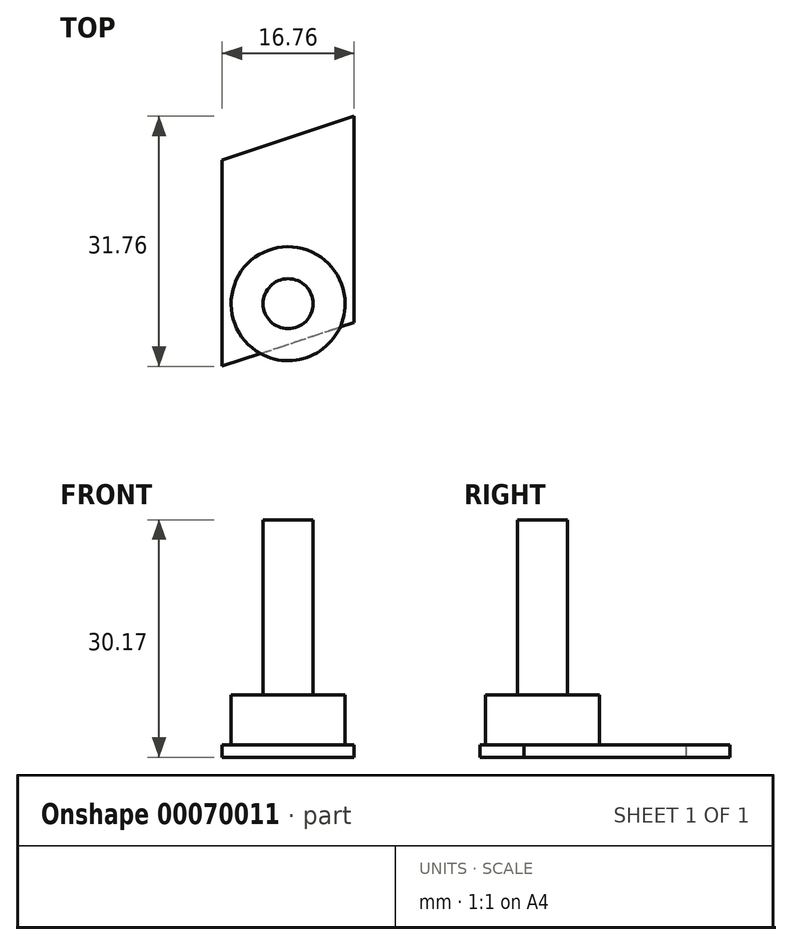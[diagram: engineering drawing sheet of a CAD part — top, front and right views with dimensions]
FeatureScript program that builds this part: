
annotation { "Feature Type Name" : "Feature", "Feature Type Description" : "" }
export const myFeature = defineFeature(function(context is Context, id is Id, definition is map)
    precondition{}
    {
        {
            var Q0;
            Q0=qCreatedBy(makeId("Top.planeOp"),FACE);
            var sketch = newSketch(context, id + "F0", { "sketchPlane" : qUnion([Q0])});
            skLineSegment(sketch, "E0.bottom", {"start": v(-8.38, 15.88) * mm, "end": v(8.38, 15.88) * mm, "construction": true});
            skLineSegment(sketch, "E0.top", {"start": v(-8.38, -15.88) * mm, "end": v(8.38, -15.88) * mm, "construction": true});
            skLineSegment(sketch, "E0.left", {"start": v(-8.38, 15.88) * mm, "end": v(-8.38, -15.88) * mm, "construction": true});
            skLineSegment(sketch, "E0.right", {"start": v(8.38, 15.88) * mm, "end": v(8.38, -15.88) * mm, "construction": true});
            skPoint(sketch, "E0.middle", {"position": v(0, 0) * mm});
            skLineSegment(sketch, "E1", {"start": v(8.38, 15.88) * mm, "end": v(-8.38, 10.32) * mm});
            skLineSegment(sketch, "E2", {"start": v(-8.38, -15.88) * mm, "end": v(8.38, -10.32) * mm});
            skLineSegment(sketch, "E3", {"start": v(-8.38, 10.32) * mm, "end": v(-8.38, -15.88) * mm});
            skLineSegment(sketch, "E4", {"start": v(8.38, -10.32) * mm, "end": v(8.38, 15.88) * mm});
            skCircle(sketch, "E5", {"center": v(0, -7.94) * mm, "radius": 7.24 * mm, "construction": true});
            skCircle(sketch, "E6", {"center": v(0, -7.94) * mm, "radius": 3.18 * mm, "construction": true});
            skLineSegment(sketch, "E7", {"start": v(-8.38, 0) * mm, "end": v(8.38, 0) * mm, "construction": true});
            skLineSegment(sketch, "E8", {"start": v(0, 0) * mm, "end": v(0, -15.88) * mm, "construction": true});
            skSolve(sketch);
        }
        {
            var Q0;
            Q0 = qSketchRegion(id + "F0", true);
            extrude(context, id + "F1", {"entities" : qUnion([Q0]), "oppositeDirection" : true, "depth" : 1.59 * mm});
        }
        {
            var Q0;
            Q0=makeQuery(id+"F0.imprint","IMPRINT",FACE,{"disambiguationData":[TD([[makeQuery(id+"F0.imprint","IMPRINT",EDGE,{"derivedFrom":sQuery(id+"F0.wireOp",EDGE,"E1")}),1.0]])]});
            var sketch = newSketch(context, id + "F2", { "sketchPlane" : qUnion([Q0])});
            skCircle(sketch, "E9.0", {"center": v(0, -7.94) * mm, "radius": 7.24 * mm});
            skSolve(sketch);
        }
        {
            var Q0;
            {var subQ0=sQuery(id+"F2.wireOp",EDGE,"E9.0");var subQ1=makeQuery(id+"F0.imprint","IMPRINT",EDGE,{"derivedFrom":sQuery(id+"F0.wireOp",EDGE,"E2")});var subQ2=makeQuery(id+"F2.imprint","INTERSECT",VERTEX,{"disambiguationData":[OD(0.0)],"derivedFrom":[subQ1,subQ0]});Q0=makeQuery(id+"F2.imprint","IMPRINT",FACE,{"disambiguationData":[TD([[makeQuery(id+"F2.imprint","IMPRINT",EDGE,{"disambiguationData":[TD([[subQ2,1.0]])],"derivedFrom":subQ0}),1.0]])]});}
            var Q1;
            {var subQ0=sQuery(id+"F2.wireOp",EDGE,"E9.0");var subQ1=makeQuery(id+"F0.imprint","IMPRINT",EDGE,{"derivedFrom":sQuery(id+"F0.wireOp",EDGE,"E2")});var subQ2=makeQuery(id+"F2.imprint","INTERSECT",VERTEX,{"disambiguationData":[OD(0.0)],"derivedFrom":[subQ1,subQ0]});Q1=makeQuery(id+"F2.imprint","IMPRINT",FACE,{"disambiguationData":[TD([[makeQuery(id+"F2.imprint","IMPRINT",EDGE,{"disambiguationData":[TD([[subQ2,-1.0]])],"derivedFrom":subQ0}),1.0]])]});}
            var Q2;
            Q2=sQuery(id+"F2.wireOp",EDGE,"E9.0");
            extrude(context, id + "F3", {"entities" : qUnion([Q0, Q1]), "operationType" : NewBodyOperationType.ADD, "surfaceEntities" : qUnion([Q2]), "depth" : 6.35 * mm});
        }
        {
            var Q0;
            Q0=qCreatedBy(makeId("Top.planeOp"),FACE);
            var sketch = newSketch(context, id + "F4", { "sketchPlane" : qUnion([Q0])});
            skCircle(sketch, "E10.0", {"center": v(0, -7.94) * mm, "radius": 3.18 * mm});
            skSolve(sketch);
        }
        {
            var Q0;
            Q0 = qSketchRegion(id + "F4", true);
            extrude(context, id + "F5", {"entities" : qUnion([Q0]), "operationType" : NewBodyOperationType.ADD, "depth" : 28.57 * mm});
        }
    });
